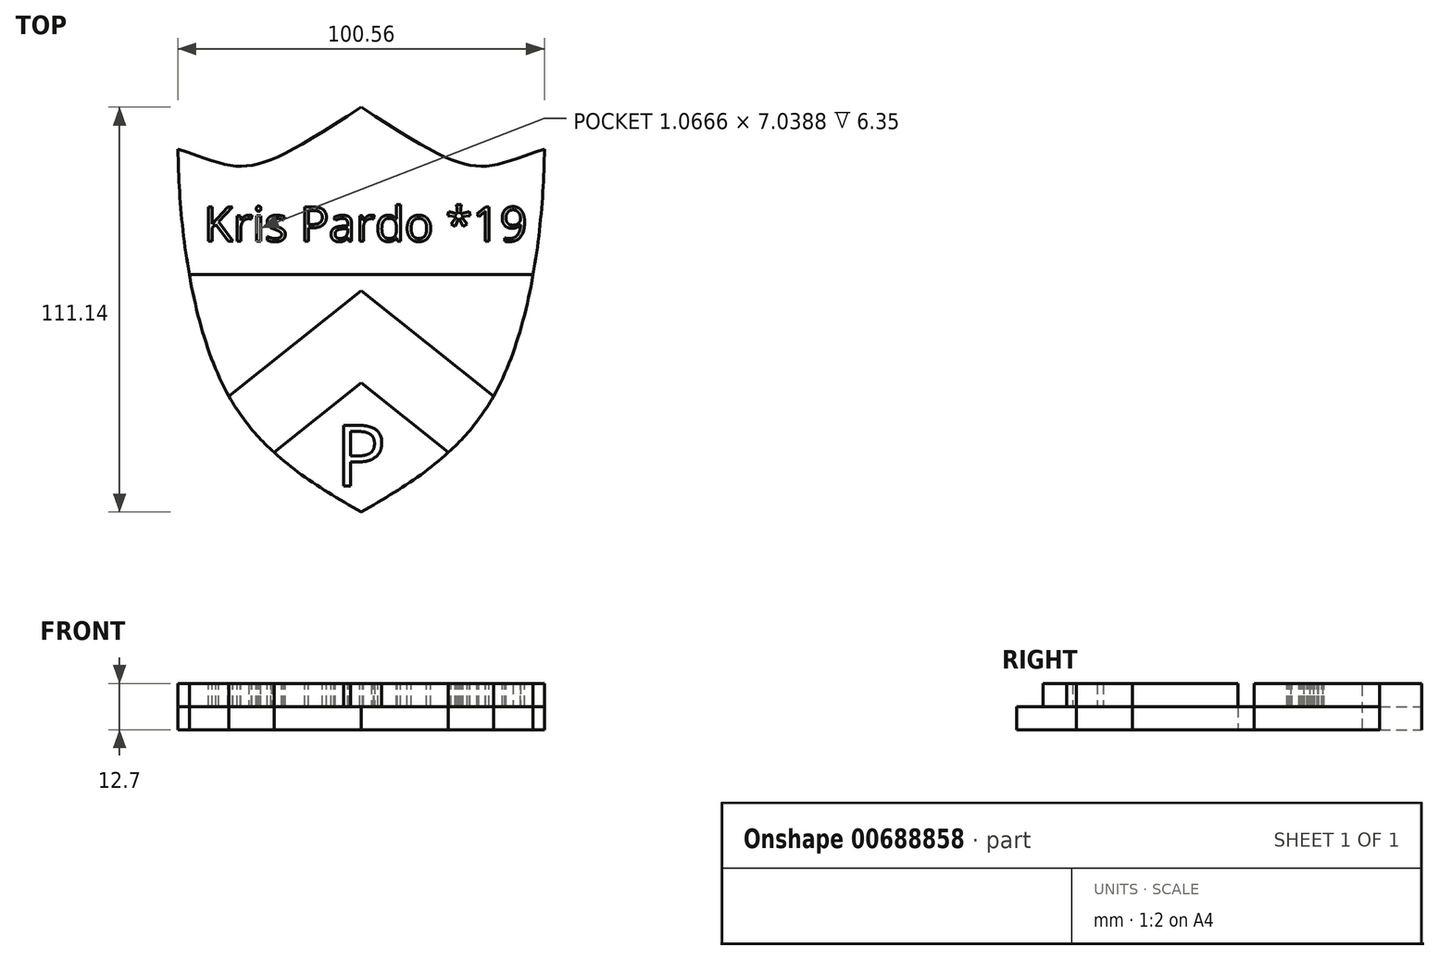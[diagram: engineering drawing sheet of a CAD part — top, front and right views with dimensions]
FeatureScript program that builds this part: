
annotation { "Feature Type Name" : "Feature", "Feature Type Description" : "" }
export const myFeature = defineFeature(function(context is Context, id is Id, definition is map)
    precondition{}
    {
        {
            var Q0;
            Q0=qCreatedBy(makeId("Top.planeOp"),FACE);
            var sketch = newSketch(context, id + "F0", { "sketchPlane" : qUnion([Q0])});
            skFitSpline(sketch, "E0", {"points": [v(-50.28, 44.36) * mm, v(-31.91, 39.7) * mm, v(0, 55.88) * mm], "startDerivative": vector(66.05, -22.58) * mm, "endDerivative": vector(91.02, 59.4) * mm});
            skFitSpline(sketch, "E1", {"points": [v(-50.28, 44.36) * mm, v(-36.27, -23.5) * mm, v(0, -55.26) * mm], "startDerivative": vector(1.71, -125.04) * mm, "endDerivative": vector(100.27, -57.89) * mm});
            skFitSpline(sketch, "E2.MirrorCS", {"points": [v(50.28, 44.36) * mm, v(31.91, 39.7) * mm, v(0, 55.88) * mm], "startDerivative": vector(-66.05, -22.58) * mm, "endDerivative": vector(-91.02, 59.4) * mm});
            skFitSpline(sketch, "E3.MirrorCS", {"points": [v(50.28, 44.36) * mm, v(36.27, -23.5) * mm, v(0, -55.26) * mm], "startDerivative": vector(-1.71, -125.04) * mm, "endDerivative": vector(-100.27, -57.89) * mm});
            skLineSegment(sketch, "E4", {"start": v(-47.15, 9.92) * mm, "end": v(47.15, 9.92) * mm});
            skLineSegment(sketch, "E5", {"start": v(-36.27, -23.5) * mm, "end": v(0, 5.45) * mm});
            skLineSegment(sketch, "E6", {"start": v(-23.93, -38.87) * mm, "end": v(0, -19.77) * mm});
            skLineSegment(sketch, "E7.MirrorCS", {"start": v(36.27, -23.5) * mm, "end": v(0, 5.45) * mm});
            skLineSegment(sketch, "E8.MirrorCS", {"start": v(23.93, -38.87) * mm, "end": v(0, -19.77) * mm});
            skSolve(sketch);
        }
        {
            var Q0;
            {var subQ1=sQuery(id+"F0.wireOp",EDGE,"E5");Q0=makeQuery(id+"F0.imprint","IMPRINT",FACE,{"disambiguationData":[TD([[makeQuery(id+"F0.imprint","IMPRINT",EDGE,{"derivedFrom":subQ1}),-1.0]])]});}
            extrude(context, id + "F1", {"entities" : qUnion([Q0]), "depth" : 12.7 * mm, "offsetDistance" : 25.4 * mm});
        }
        {
            var Q0;
            {var subQ4=sQuery(id+"F0.wireOp",EDGE,"E0");Q0=makeQuery(id+"F0.imprint","IMPRINT",FACE,{"disambiguationData":[TD([[makeQuery(id+"F0.imprint","IMPRINT",EDGE,{"derivedFrom":subQ4}),-1.0]])]});}
            extrude(context, id + "F2", {"entities" : qUnion([Q0]), "depth" : 12.7 * mm, "offsetDistance" : 25.4 * mm});
        }
        {
            var Q0;
            {var subQ1=sQuery(id+"F0.wireOp",EDGE,"E4");Q0=makeQuery(id+"F0.imprint","IMPRINT",FACE,{"disambiguationData":[TD([[makeQuery(id+"F0.imprint","IMPRINT",EDGE,{"derivedFrom":subQ1}),-1.0]])]});}
            var Q1;
            {var subQ3=sQuery(id+"F0.wireOp",EDGE,"E6");Q1=makeQuery(id+"F0.imprint","IMPRINT",FACE,{"disambiguationData":[TD([[makeQuery(id+"F0.imprint","IMPRINT",EDGE,{"derivedFrom":subQ3}),-1.0]])]});}
            extrude(context, id + "F3", {"entities" : qUnion([Q0, Q1]), "depth" : 6.35 * mm, "offsetDistance" : 25.4 * mm});
        }
        {
            var Q0;
            Q0 = qSketchRegion(id + "F0", true);
            extrude(context, id + "F4", {"entities" : qUnion([Q0]), "depth" : 6.35 * mm, "offsetDistance" : 25.4 * mm});
        }
        {
            var Q0;
            Q0=makeQuery(id+"F2.opExtrude","CAP_FACE",FACE,{"disambiguationData":[OSD([sQuery(id+"F0.wireOp",EDGE,"E0"),sQuery(id+"F0.wireOp",EDGE,"E1"),sQuery(id+"F0.wireOp",EDGE,"E2.MirrorCS"),sQuery(id+"F0.wireOp",EDGE,"E3.MirrorCS"),sQuery(id+"F0.wireOp",EDGE,"E4")])],"isStart":false});
            var sketch = newSketch(context, id + "F5", { "sketchPlane" : qUnion([Q0])});
            skText(sketch, "E9", { "text": "Kris Pardo *19", "fontName": "OpenSans-Regular.ttf"});
            const initialGuessF5  = {"E9": [-0.04326, 0.01907, 1, 0, 0.00947]};
            skSetInitialGuess(sketch, initialGuessF5);
            skSolve(sketch);
        }
        {
            var Q0;
            Q0 = qSketchRegion(id + "F5", true);
            extrude(context, id + "F6", {"entities" : qUnion([Q0]), "operationType" : NewBodyOperationType.REMOVE, "oppositeDirection" : true, "depth" : 6.35 * mm, "offsetDistance" : 25.4 * mm});
        }
        {
            var Q0;
            Q0=makeQuery(id+"F3.opExtrude","CAP_FACE",FACE,{"disambiguationData":[OSD([sQuery(id+"F0.wireOp",EDGE,"E1"),sQuery(id+"F0.wireOp",EDGE,"E3.MirrorCS"),sQuery(id+"F0.wireOp",EDGE,"E6"),sQuery(id+"F0.wireOp",EDGE,"E8.MirrorCS")])],"isStart":false});
            var sketch = newSketch(context, id + "F7", { "sketchPlane" : qUnion([Q0])});
            skText(sketch, "E10", { "text": "P", "fontName": "OpenSans-Regular.ttf"});
            const initialGuessF7  = {"E10": [-0.00714, -0.04803, 1, 0, 0.0167]};
            skSetInitialGuess(sketch, initialGuessF7);
            skSolve(sketch);
        }
        {
            var Q0;
            Q0 = qSketchRegion(id + "F7", true);
            extrude(context, id + "F8", {"entities" : qUnion([Q0]), "operationType" : NewBodyOperationType.ADD, "depth" : 6.35 * mm, "offsetDistance" : 25.4 * mm});
        }
    });
